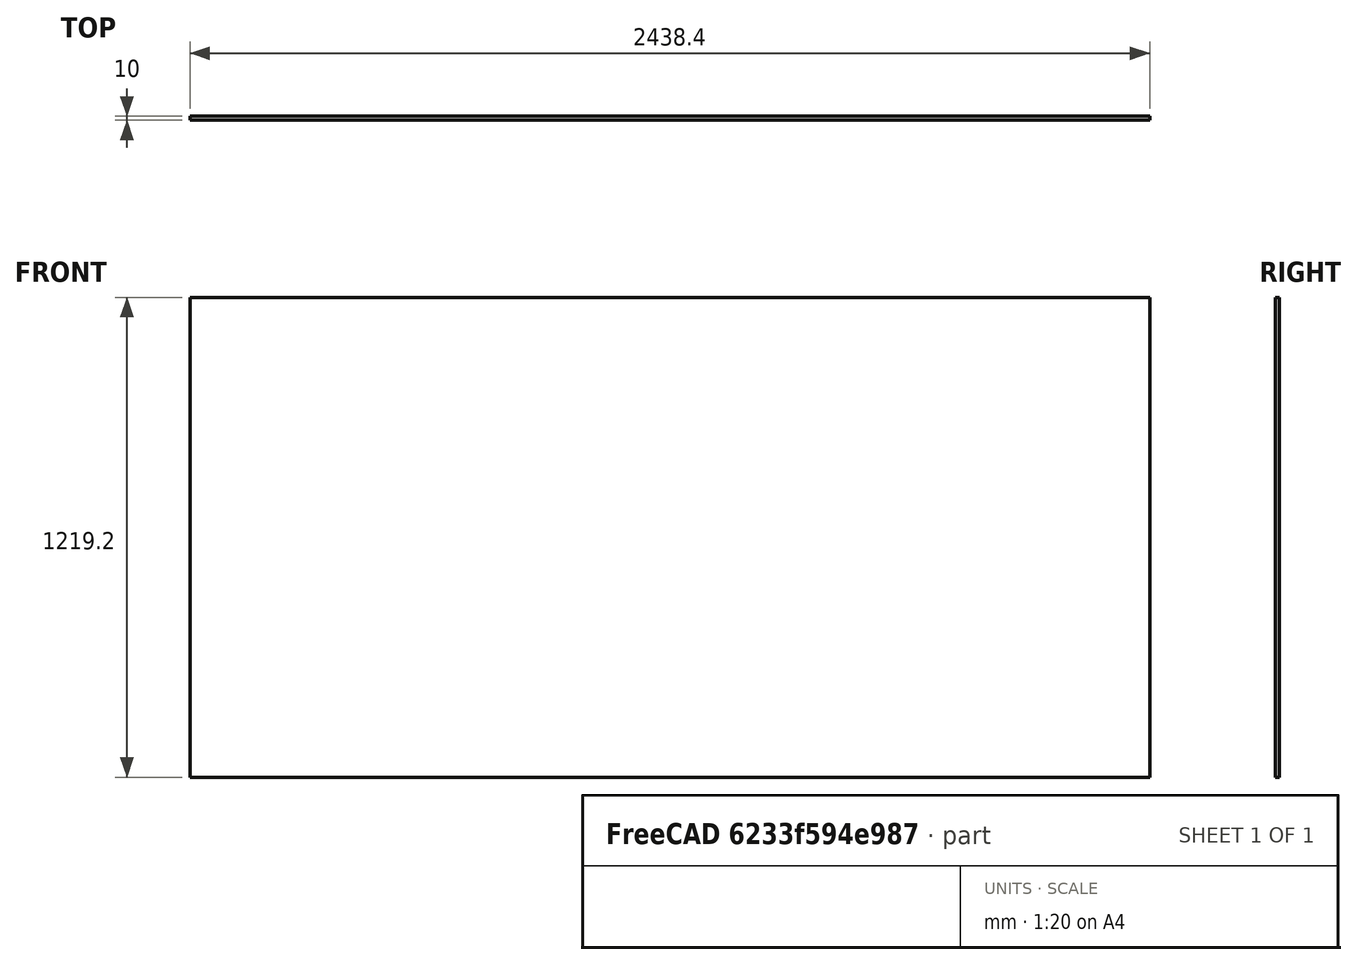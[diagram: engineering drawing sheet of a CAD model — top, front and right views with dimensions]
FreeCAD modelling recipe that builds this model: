
FCSTD DOCUMENT  (FreeCAD 0.19R24291 (Git))
Label: whiteBoard
License: All rights reserved
LicenseURL: http://en.wikipedia.org/wiki/All_rights_reserved
objects: Sketcher::SketchObject×1, PartDesign::Pad×1, PartDesign::Body×1
note: 4 computed .brp shape members not serialized (recipe doc carries the construction recipe); baked Part::Feature solids carry a one-line shape summary decoded from their .brp

FEATURE [Sketcher::SketchObject] Sketch
  FullyConstrained = true
  MapMode = 5
  Placement = pos=(0,0,0) rot=(1,0,0;1.5708rad)
  Support = -> [XZ_Plane]
  expr: Constraints[10] = 4 * 12 * 25.4
  expr: Constraints[9] = 8 * 12 * 25.4
  sketch-geometry (4):
    g0: LineSegment StartX=0 StartY=0 StartZ=0 EndX=2438.4 EndY=0 EndZ=0
    g1: LineSegment StartX=2438.4 StartY=0 StartZ=0 EndX=2438.4 EndY=1219.2 EndZ=0
    g2: LineSegment StartX=2438.4 StartY=1219.2 StartZ=0 EndX=0 EndY=1219.2 EndZ=0
    g3: LineSegment StartX=0 StartY=1219.2 StartZ=0 EndX=0 EndY=0 EndZ=0
  constraints (11):
    c: Coincident(g0,g1)
    c: Coincident(g1,g2)
    c: Coincident(g2,g3)
    c: Coincident(g3,g0)
    c: Horizontal(g0)
    c: Horizontal(g2)
    c: Vertical(g1)
    c: Vertical(g3)
    c: Coincident(g0,g-1)
    c: DistanceX(g0,g0) = 2438.4
    c: DistanceY(g3,g3) = 1219.2
FEATURE [PartDesign::Pad] Pad
  Direction = (1,1,1)
  Length = 10
  Length2 = 100
  Placement = pos=(0,0,0) rot=(1,0,0;1.5708rad)
  Profile = -> Sketch
  Type = 0
FEATURE [PartDesign::Body] Body
  Group = -> [Sketch,Pad]
  Origin = -> Origin
  Tip = -> Pad
